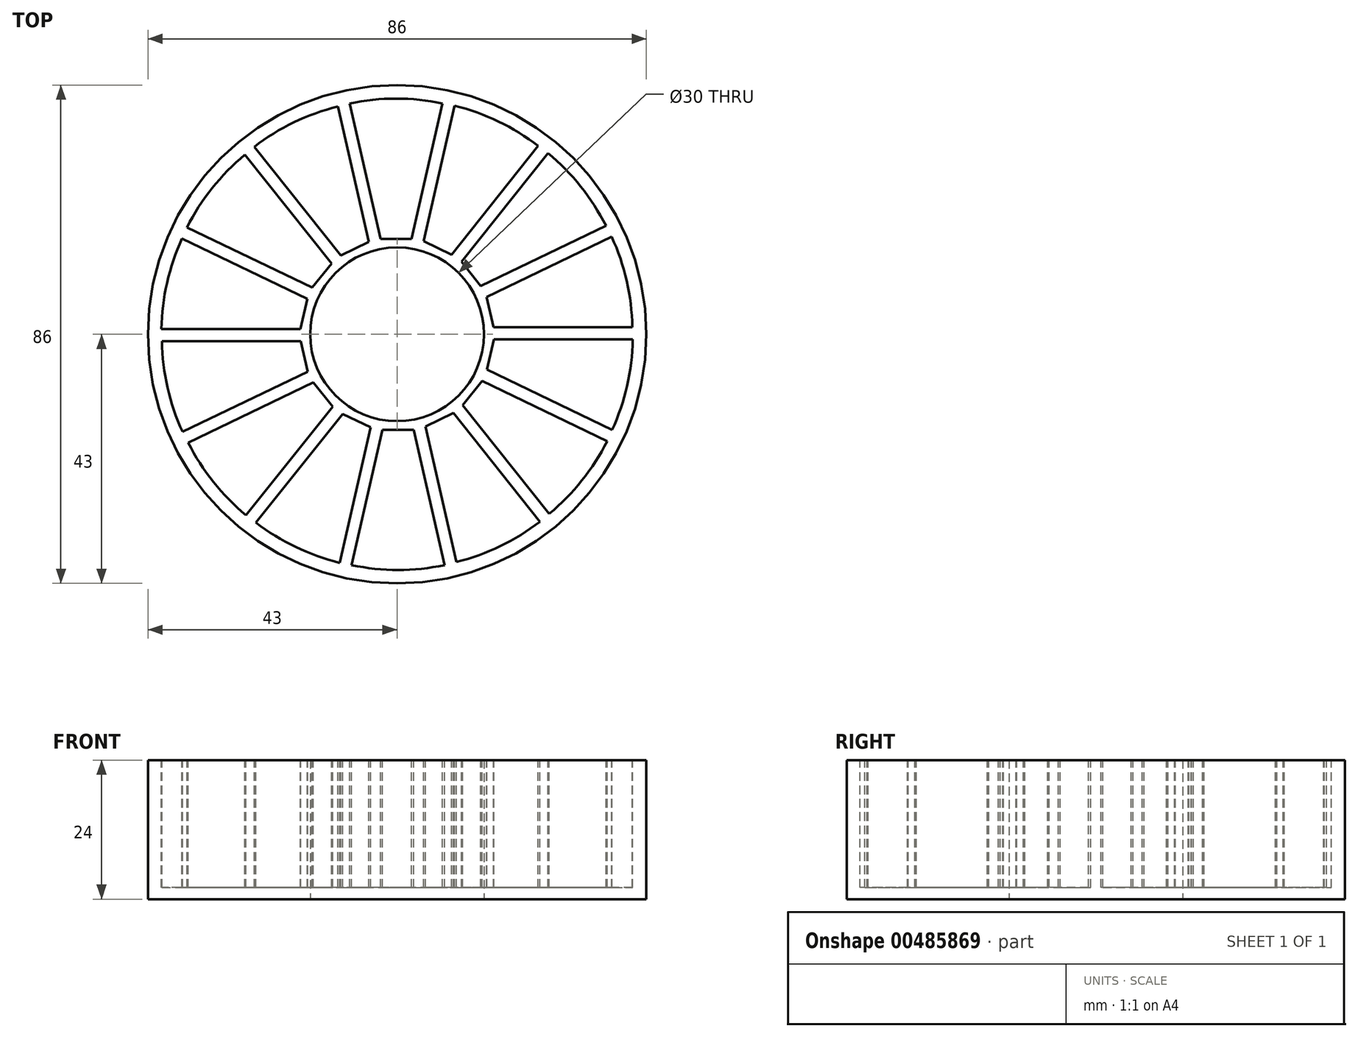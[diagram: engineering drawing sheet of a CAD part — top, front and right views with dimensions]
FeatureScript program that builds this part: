
annotation { "Feature Type Name" : "Feature", "Feature Type Description" : "" }
export const myFeature = defineFeature(function(context is Context, id is Id, definition is map)
    precondition{}
    {
        {
            var Q0;
            Q0=qCreatedBy(makeId("Top.planeOp"),FACE);
            var sketch = newSketch(context, id + "F0", { "sketchPlane" : qUnion([Q0])});
            skCircle(sketch, "E0", {"center": v(0, 0) * mm, "radius": 43 * mm});
            skCircle(sketch, "E1", {"center": v(0, 0) * mm, "radius": 15 * mm});
            skSolve(sketch);
        }
        {
            var Q0;
            Q0=makeQuery(id+"F0.imprint","IMPRINT",FACE,{"disambiguationData":[TD([[makeQuery(id+"F0.imprint","IMPRINT",EDGE,{"derivedFrom":sQuery(id+"F0.wireOp",EDGE,"E0")}),1.0]])]});
            extrude(context, id + "F1", {"entities" : qUnion([Q0]), "depth" : 24 * mm, "offsetDistance" : 25 * mm});
        }
        {
            var Q0;
            Q0=makeQuery(id+"F1.opExtrude","CAP_FACE",FACE,{"disambiguationData":[OSD([sQuery(id+"F0.wireOp",EDGE,"E0"),sQuery(id+"F0.wireOp",EDGE,"E1")])],"isStart":false});
            var sketch = newSketch(context, id + "F2", { "sketchPlane" : qUnion([Q0])});
            skLineSegment(sketch, "E2", {"start": v(0, 0) * mm, "end": v(8.61, 37.75) * mm, "construction": true});
            skLineSegment(sketch, "E3", {"start": v(0, 0) * mm, "end": v(-8.05, 35.3) * mm, "construction": true});
            skLineSegment(sketch, "E4", {"start": v(7.84, 39.85) * mm, "end": v(2.5, 16.47) * mm});
            skLineSegment(sketch, "E5", {"start": v(2.5, 16.47) * mm, "end": v(-2.84, 16.47) * mm});
            skLineSegment(sketch, "E6", {"start": v(-2.84, 16.47) * mm, "end": v(-8.18, 39.85) * mm});
            skArc(sketch, "E7", {"start": v(7.84, 39.85) * mm, "mid": v(-0.17, 40.68) * mm, "end": v(-8.18, 39.85) * mm});
            skArc(sketch, "E8.1.0", {"start": v(-10.23, 39.3) * mm, "mid": v(-17.8, 36.58) * mm, "end": v(-24.66, 32.36) * mm});
            skLineSegment(sketch, "E8.1.1", {"start": v(-9.7, 13.6) * mm, "end": v(-24.66, 32.36) * mm});
            skLineSegment(sketch, "E8.1.2", {"start": v(-10.23, 39.3) * mm, "end": v(-4.89, 15.93) * mm});
            skLineSegment(sketch, "E8.1.3", {"start": v(-4.89, 15.93) * mm, "end": v(-9.7, 13.6) * mm});
            skArc(sketch, "E8.2.0", {"start": v(-26.27, 30.98) * mm, "mid": v(-31.9, 25.23) * mm, "end": v(-36.26, 18.45) * mm});
            skLineSegment(sketch, "E8.2.1", {"start": v(-14.65, 8.04) * mm, "end": v(-36.26, 18.45) * mm});
            skLineSegment(sketch, "E8.2.2", {"start": v(-26.27, 30.98) * mm, "end": v(-11.31, 12.23) * mm});
            skLineSegment(sketch, "E8.2.3", {"start": v(-11.31, 12.23) * mm, "end": v(-14.65, 8.04) * mm});
            skArc(sketch, "E8.3.0", {"start": v(-37.1, 16.51) * mm, "mid": v(-39.7, 8.89) * mm, "end": v(-40.67, 0.9) * mm});
            skLineSegment(sketch, "E8.3.1", {"start": v(-16.69, 0.9) * mm, "end": v(-40.67, 0.9) * mm});
            skLineSegment(sketch, "E8.3.2", {"start": v(-37.1, 16.51) * mm, "end": v(-15.5, 6.11) * mm});
            skLineSegment(sketch, "E8.3.3", {"start": v(-15.5, 6.11) * mm, "end": v(-16.69, 0.9) * mm});
            skArc(sketch, "E8.4.0", {"start": v(-40.6, -1.22) * mm, "mid": v(-39.62, -9.22) * mm, "end": v(-37.03, -16.84) * mm});
            skLineSegment(sketch, "E8.4.1", {"start": v(-15.42, -6.44) * mm, "end": v(-37.03, -16.84) * mm});
            skLineSegment(sketch, "E8.4.2", {"start": v(-40.6, -1.22) * mm, "end": v(-16.61, -1.22) * mm});
            skLineSegment(sketch, "E8.4.3", {"start": v(-16.61, -1.22) * mm, "end": v(-15.42, -6.44) * mm});
            skArc(sketch, "E8.5.0", {"start": v(-36.05, -18.72) * mm, "mid": v(-31.7, -25.5) * mm, "end": v(-26.06, -31.24) * mm});
            skLineSegment(sketch, "E8.5.1", {"start": v(-11.1, -12.5) * mm, "end": v(-26.06, -31.24) * mm});
            skLineSegment(sketch, "E8.5.2", {"start": v(-36.05, -18.72) * mm, "end": v(-14.44, -8.3) * mm});
            skLineSegment(sketch, "E8.5.3", {"start": v(-14.44, -8.3) * mm, "end": v(-11.1, -12.5) * mm});
            skArc(sketch, "E8.6.0", {"start": v(-24.36, -32.5) * mm, "mid": v(-17.5, -36.72) * mm, "end": v(-9.92, -39.45) * mm});
            skLineSegment(sketch, "E8.6.1", {"start": v(-4.58, -16.07) * mm, "end": v(-9.92, -39.45) * mm});
            skLineSegment(sketch, "E8.6.2", {"start": v(-24.36, -32.5) * mm, "end": v(-9.4, -13.75) * mm});
            skLineSegment(sketch, "E8.6.3", {"start": v(-9.4, -13.75) * mm, "end": v(-4.58, -16.07) * mm});
            skArc(sketch, "E8.7.0", {"start": v(-7.84, -39.85) * mm, "mid": v(0.17, -40.68) * mm, "end": v(8.18, -39.85) * mm});
            skLineSegment(sketch, "E8.7.1", {"start": v(2.84, -16.47) * mm, "end": v(8.18, -39.85) * mm});
            skLineSegment(sketch, "E8.7.2", {"start": v(-7.84, -39.85) * mm, "end": v(-2.5, -16.47) * mm});
            skLineSegment(sketch, "E8.7.3", {"start": v(-2.5, -16.47) * mm, "end": v(2.84, -16.47) * mm});
            skArc(sketch, "E8.8.0", {"start": v(10.23, -39.3) * mm, "mid": v(17.8, -36.58) * mm, "end": v(24.66, -32.36) * mm});
            skLineSegment(sketch, "E8.8.1", {"start": v(9.7, -13.6) * mm, "end": v(24.66, -32.36) * mm});
            skLineSegment(sketch, "E8.8.2", {"start": v(10.23, -39.3) * mm, "end": v(4.89, -15.93) * mm});
            skLineSegment(sketch, "E8.8.3", {"start": v(4.89, -15.93) * mm, "end": v(9.7, -13.6) * mm});
            skArc(sketch, "E8.9.0", {"start": v(26.27, -30.98) * mm, "mid": v(31.9, -25.23) * mm, "end": v(36.26, -18.45) * mm});
            skLineSegment(sketch, "E8.9.1", {"start": v(14.65, -8.04) * mm, "end": v(36.26, -18.45) * mm});
            skLineSegment(sketch, "E8.9.2", {"start": v(26.27, -30.98) * mm, "end": v(11.31, -12.23) * mm});
            skLineSegment(sketch, "E8.9.3", {"start": v(11.31, -12.23) * mm, "end": v(14.65, -8.04) * mm});
            skArc(sketch, "E8.10.0", {"start": v(37.1, -16.51) * mm, "mid": v(39.7, -8.89) * mm, "end": v(40.67, -0.9) * mm});
            skLineSegment(sketch, "E8.10.1", {"start": v(16.69, -0.9) * mm, "end": v(40.67, -0.9) * mm});
            skLineSegment(sketch, "E8.10.2", {"start": v(37.1, -16.51) * mm, "end": v(15.5, -6.11) * mm});
            skLineSegment(sketch, "E8.10.3", {"start": v(15.5, -6.11) * mm, "end": v(16.69, -0.9) * mm});
            skArc(sketch, "E8.11.0", {"start": v(40.6, 1.22) * mm, "mid": v(39.62, 9.22) * mm, "end": v(37.03, 16.84) * mm});
            skLineSegment(sketch, "E8.11.1", {"start": v(15.42, 6.44) * mm, "end": v(37.03, 16.84) * mm});
            skLineSegment(sketch, "E8.11.2", {"start": v(40.6, 1.22) * mm, "end": v(16.61, 1.22) * mm});
            skLineSegment(sketch, "E8.11.3", {"start": v(16.61, 1.22) * mm, "end": v(15.42, 6.44) * mm});
            skArc(sketch, "E8.12.0", {"start": v(36.05, 18.72) * mm, "mid": v(31.7, 25.5) * mm, "end": v(26.06, 31.24) * mm});
            skLineSegment(sketch, "E8.12.1", {"start": v(11.1, 12.5) * mm, "end": v(26.06, 31.24) * mm});
            skLineSegment(sketch, "E8.12.2", {"start": v(36.05, 18.72) * mm, "end": v(14.44, 8.3) * mm});
            skLineSegment(sketch, "E8.12.3", {"start": v(14.44, 8.3) * mm, "end": v(11.1, 12.5) * mm});
            skArc(sketch, "E8.13.0", {"start": v(24.36, 32.5) * mm, "mid": v(17.5, 36.72) * mm, "end": v(9.92, 39.45) * mm});
            skLineSegment(sketch, "E8.13.1", {"start": v(4.58, 16.07) * mm, "end": v(9.92, 39.45) * mm});
            skLineSegment(sketch, "E8.13.2", {"start": v(24.36, 32.5) * mm, "end": v(9.4, 13.75) * mm});
            skLineSegment(sketch, "E8.13.3", {"start": v(9.4, 13.75) * mm, "end": v(4.58, 16.07) * mm});
            skPoint(sketch, "E8.center", {"position": v(0, 0) * mm});
            skSolve(sketch);
        }
        {
            var Q0;
            Q0=makeQuery(id+"F2.imprint","IMPRINT",FACE,{"disambiguationData":[TD([[makeQuery(id+"F2.imprint","IMPRINT",EDGE,{"derivedFrom":sQuery(id+"F2.wireOp",EDGE,"E8.2.0")}),1.0]])]});
            var Q1;
            Q1=makeQuery(id+"F2.imprint","IMPRINT",FACE,{"disambiguationData":[TD([[makeQuery(id+"F2.imprint","IMPRINT",EDGE,{"derivedFrom":sQuery(id+"F2.wireOp",EDGE,"E8.1.0")}),1.0]])]});
            var Q2;
            Q2=makeQuery(id+"F2.imprint","IMPRINT",FACE,{"disambiguationData":[TD([[makeQuery(id+"F2.imprint","IMPRINT",EDGE,{"derivedFrom":sQuery(id+"F2.wireOp",EDGE,"E4")}),-1.0]])]});
            var Q3;
            Q3=makeQuery(id+"F2.imprint","IMPRINT",FACE,{"disambiguationData":[TD([[makeQuery(id+"F2.imprint","IMPRINT",EDGE,{"derivedFrom":sQuery(id+"F2.wireOp",EDGE,"E8.13.0")}),1.0]])]});
            var Q4;
            Q4=makeQuery(id+"F2.imprint","IMPRINT",FACE,{"disambiguationData":[TD([[makeQuery(id+"F2.imprint","IMPRINT",EDGE,{"derivedFrom":sQuery(id+"F2.wireOp",EDGE,"E8.12.0")}),1.0]])]});
            var Q5;
            Q5=makeQuery(id+"F2.imprint","IMPRINT",FACE,{"disambiguationData":[TD([[makeQuery(id+"F2.imprint","IMPRINT",EDGE,{"derivedFrom":sQuery(id+"F2.wireOp",EDGE,"E8.11.0")}),1.0]])]});
            var Q6;
            Q6=makeQuery(id+"F2.imprint","IMPRINT",FACE,{"disambiguationData":[TD([[makeQuery(id+"F2.imprint","IMPRINT",EDGE,{"derivedFrom":sQuery(id+"F2.wireOp",EDGE,"E8.10.0")}),1.0]])]});
            var Q7;
            Q7=makeQuery(id+"F2.imprint","IMPRINT",FACE,{"disambiguationData":[TD([[makeQuery(id+"F2.imprint","IMPRINT",EDGE,{"derivedFrom":sQuery(id+"F2.wireOp",EDGE,"E8.9.0")}),1.0]])]});
            var Q8;
            Q8=makeQuery(id+"F2.imprint","IMPRINT",FACE,{"disambiguationData":[TD([[makeQuery(id+"F2.imprint","IMPRINT",EDGE,{"derivedFrom":sQuery(id+"F2.wireOp",EDGE,"E8.8.0")}),1.0]])]});
            var Q9;
            Q9=makeQuery(id+"F2.imprint","IMPRINT",FACE,{"disambiguationData":[TD([[makeQuery(id+"F2.imprint","IMPRINT",EDGE,{"derivedFrom":sQuery(id+"F2.wireOp",EDGE,"E8.7.0")}),1.0]])]});
            var Q10;
            Q10=makeQuery(id+"F2.imprint","IMPRINT",FACE,{"disambiguationData":[TD([[makeQuery(id+"F2.imprint","IMPRINT",EDGE,{"derivedFrom":sQuery(id+"F2.wireOp",EDGE,"E8.6.0")}),1.0]])]});
            var Q11;
            Q11=makeQuery(id+"F2.imprint","IMPRINT",FACE,{"disambiguationData":[TD([[makeQuery(id+"F2.imprint","IMPRINT",EDGE,{"derivedFrom":sQuery(id+"F2.wireOp",EDGE,"E8.5.0")}),1.0]])]});
            var Q12;
            Q12=makeQuery(id+"F2.imprint","IMPRINT",FACE,{"disambiguationData":[TD([[makeQuery(id+"F2.imprint","IMPRINT",EDGE,{"derivedFrom":sQuery(id+"F2.wireOp",EDGE,"E8.4.0")}),1.0]])]});
            var Q13;
            Q13=makeQuery(id+"F2.imprint","IMPRINT",FACE,{"disambiguationData":[TD([[makeQuery(id+"F2.imprint","IMPRINT",EDGE,{"derivedFrom":sQuery(id+"F2.wireOp",EDGE,"E8.3.0")}),1.0]])]});
            extrude(context, id + "F3", {"entities" : qUnion([Q0, Q1, Q2, Q3, Q4, Q5, Q6, Q7, Q8, Q9, Q10, Q11, Q12, Q13]), "operationType" : NewBodyOperationType.REMOVE, "oppositeDirection" : true, "depth" : 22 * mm, "offsetDistance" : 25 * mm});
        }
    });
